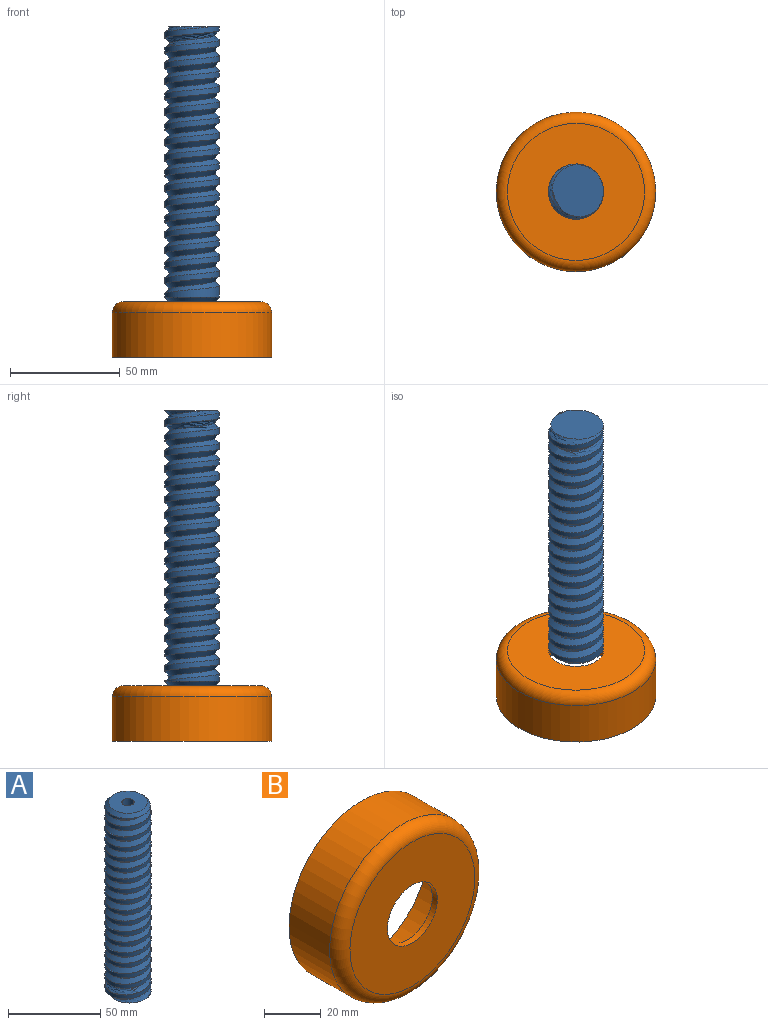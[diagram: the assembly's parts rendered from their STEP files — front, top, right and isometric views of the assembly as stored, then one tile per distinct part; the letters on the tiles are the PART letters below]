
ASSEMBLY  parts=2 mates=1
PART A: 10 faces, bbox 31.2x27.4x130.9 mm
  f0: cylinder r=12.5mm len=123.4mm, axis (0,0,-1), area 1871.5mm2, adj f1,f3,f4,f5,f9
  f1: plane 25.23x24.48mm, normal (0,0,-1), area 432.2mm2, adj f0,f2,f3,f9
  f2: bspline ~127.27x28.25mm, area 3937.4mm2, adj f1,f3,f4,f9
  f3: bspline ~121.33x29.92mm, area 357.5mm2, adj f0,f1,f2,f4
  f4: plane 3.65x2.36mm, normal (0,-1,0), area 4.7mm2, adj f0,f2,f3,f5,f9
  f5: cone r=10.5mm half-angle=45deg, axis (0,0,-1), area -191.4mm2, adj f0,f4,f6,f9
  f6: plane 21x21mm, normal (0,0,1), area 312.1mm2, adj f5,f7
  f7: cylinder r=3.3mm len=50mm, axis (0,0,1), area 1036.7mm2, adj f6,f8
  f8: cone r=0mm half-angle=59deg, axis (0,0,1), area 39.9mm2, adj f7
  f9: bspline ~128.42x29.92mm, area 3982.1mm2, adj f0,f1,f2,f4,f5
PART B: 8 faces, bbox 78.6x25.4x78.6 mm
  f0: cylinder r=36.31mm len=72.63mm, axis (0,1,0), area 4636.4mm2, adj f2,f3
  f1: plane 62.47x62.47mm, normal (0,-1,0), area 2574.1mm2, adj f3,f7
  f2: plane 72.63x72.63mm, normal (0,1,0), area 559.3mm2, adj f0,f4
  f3: torus R=31.23mm, axis (0,-1,0), area 1728.2mm2, adj f0,f1
  f4: cylinder r=33.77mm len=67.55mm, axis (0,1,0), area 4312.1mm2, adj f2,f6
  f5: plane 62.47x62.47mm, normal (0,1,0), area 2574.1mm2, adj f6,f7
  f6: torus R=31.23mm, axis (0,-1,0), area 823.6mm2, adj f4,f5
  f7: cylinder r=12.5mm len=25mm, axis (0,-1,0), area 199.5mm2, adj f1,f5
PLACE A rot(axis=(1,0,0),180deg) t=(20.37,-4.25,74.6)mm
PLACE B rot(axis=(-1,0,0),90deg) t=(20.37,-4.25,-50.8)mm fixed
MATE cylindrical A.f7 <-> B.f7  axis (0,0,-1) through (20.37,-4.25,-25.4)mm
